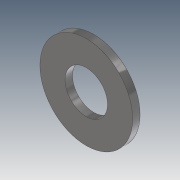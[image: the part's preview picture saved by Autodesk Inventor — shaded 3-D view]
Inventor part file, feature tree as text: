
AUTODESK INVENTOR PART (.ipt)
format: ipt  version: 2020.4 (Build 244396000, 396)  size: 99,840 bytes
history: native  units: in
note: dims shown in document units (in); Inventor stores cm internally (conversion verified against a paired STEP export)
features: extrude x1, sketch x1
ambient origin geometry x8: Origin, YZ Plane, XZ Plane, XY Plane, X Axis, Y Axis, Z Axis, Center Point
bodies: Solid1 (feature_tree)
feature tree (2):
  extrude  "Extrusion1"  Depth=0.03in
  sketch  "Sketch1"  dims[d0=0.375in d1=0.172in d2=0.03in d3=0.0in]
